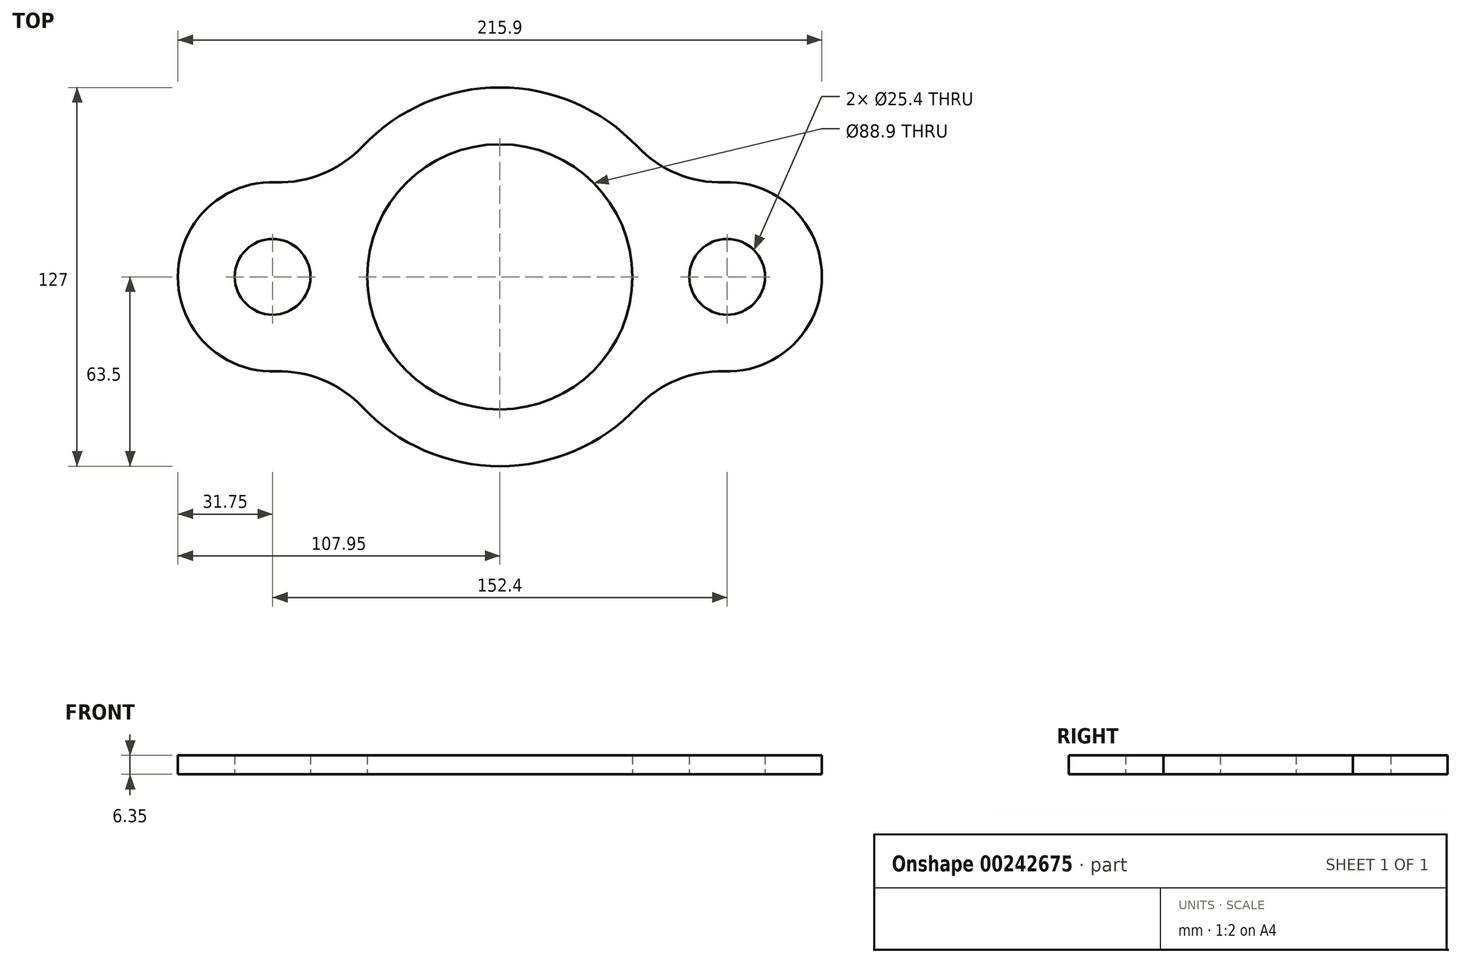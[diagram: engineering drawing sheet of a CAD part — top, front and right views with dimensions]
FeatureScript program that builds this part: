
annotation { "Feature Type Name" : "Feature", "Feature Type Description" : "" }
export const myFeature = defineFeature(function(context is Context, id is Id, definition is map)
    precondition{}
    {
        {
            var Q0;
            Q0=qCreatedBy(makeId("Top.planeOp"),FACE);
            var sketch = newSketch(context, id + "F0", { "sketchPlane" : qUnion([Q0])});
            skArc(sketch, "E0", {"start": v(-46.14, -43.63) * mm, "mid": v(0, -63.5) * mm, "end": v(46.14, -43.63) * mm});
            skCircle(sketch, "E1", {"center": v(0, 0) * mm, "radius": 44.45 * mm});
            skLineSegment(sketch, "E2", {"start": v(-63.5, 0) * mm, "end": v(-76.2, 0) * mm});
            skCircle(sketch, "E3", {"center": v(-76.2, 0) * mm, "radius": 12.7 * mm});
            skCircle(sketch, "E4", {"center": v(76.2, 0) * mm, "radius": 12.7 * mm});
            skArc(sketch, "E5", {"start": v(75.12, -31.73) * mm, "mid": v(107.95, 0) * mm, "end": v(75.12, 31.73) * mm});
            skArc(sketch, "E6", {"start": v(-75.12, 31.73) * mm, "mid": v(-107.95, 0) * mm, "end": v(-75.12, -31.73) * mm});
            skArc(sketch, "E7.trimOffspring", {"start": v(46.14, 43.63) * mm, "mid": v(0, 63.5) * mm, "end": v(-46.14, 43.63) * mm});
            skPoint(sketch, "E8.visualSharp", {"position": v(-57.94, 25.98) * mm});
            skArc(sketch, "E8.filletArc", {"start": v(-75.12, 31.73) * mm, "mid": v(-59.35, 34.56) * mm, "end": v(-46.14, 43.63) * mm});
            skPoint(sketch, "E9.visualSharp", {"position": v(57.94, 25.98) * mm});
            skArc(sketch, "E9.filletArc", {"start": v(46.14, 43.63) * mm, "mid": v(59.35, 34.56) * mm, "end": v(75.12, 31.73) * mm});
            skPoint(sketch, "E10.visualSharp", {"position": v(57.94, -25.98) * mm});
            skArc(sketch, "E10.filletArc", {"start": v(75.12, -31.73) * mm, "mid": v(59.35, -34.56) * mm, "end": v(46.14, -43.63) * mm});
            skPoint(sketch, "E11.visualSharp", {"position": v(-57.94, -25.98) * mm});
            skArc(sketch, "E11.filletArc", {"start": v(-46.14, -43.63) * mm, "mid": v(-59.35, -34.56) * mm, "end": v(-75.12, -31.73) * mm});
            skSolve(sketch);
        }
        {
            var Q0;
            Q0=makeQuery(id+"F0.imprint","IMPRINT",FACE,{"disambiguationData":[TD([[makeQuery(id+"F0.imprint","IMPRINT",EDGE,{"derivedFrom":sQuery(id+"F0.wireOp",EDGE,"E0")}),1.0]])]});
            extrude(context, id + "F1", {"entities" : qUnion([Q0]), "depth" : 6.35 * mm});
        }
    });
